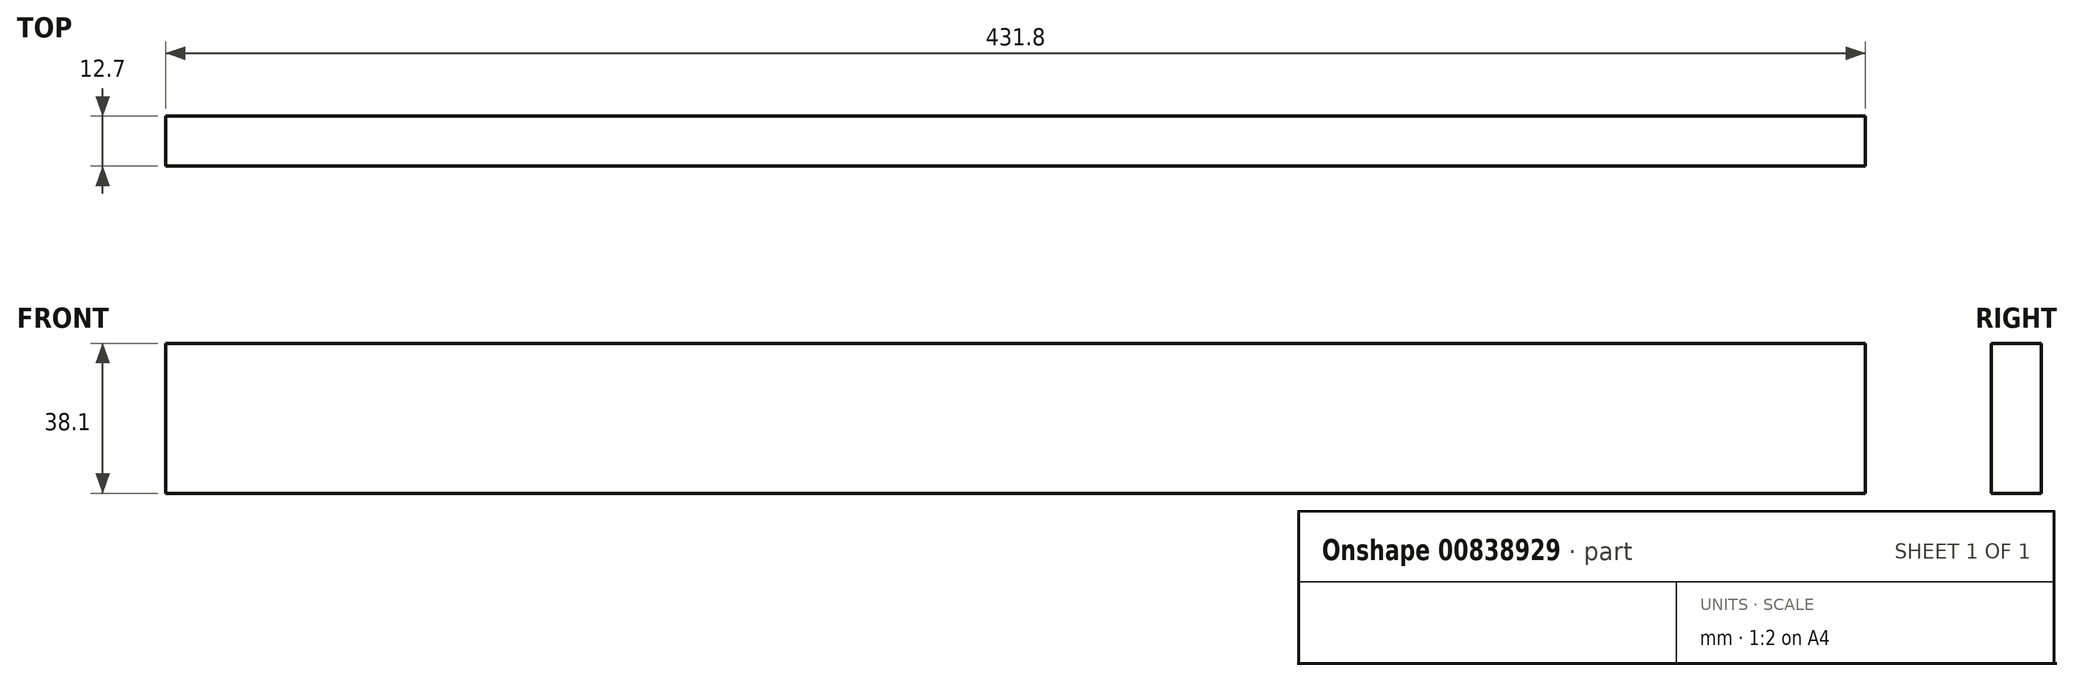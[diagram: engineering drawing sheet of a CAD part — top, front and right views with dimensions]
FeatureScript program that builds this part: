
annotation { "Feature Type Name" : "Feature", "Feature Type Description" : "" }
export const myFeature = defineFeature(function(context is Context, id is Id, definition is map)
    precondition{}
    {
        {
            var Q0;
            Q0=qCreatedBy(makeId("Front.planeOp"),FACE);
            var sketch = newSketch(context, id + "F0", { "sketchPlane" : qUnion([Q0])});
            skLineSegment(sketch, "E0", {"start": v(0, 0) * mm, "end": v(0, 38.1) * mm});
            skLineSegment(sketch, "E1", {"start": v(0, 38.1) * mm, "end": v(431.8, 38.1) * mm});
            skLineSegment(sketch, "E2", {"start": v(431.8, 38.1) * mm, "end": v(431.8, 0) * mm});
            skLineSegment(sketch, "E3", {"start": v(431.8, 0) * mm, "end": v(0, 0) * mm});
            skSolve(sketch);
        }
        {
            var Q0;
            Q0 = qSketchRegion(id + "F0", true);
            extrude(context, id + "F1", {"entities" : qUnion([Q0]), "depth" : 12.7 * mm, "offsetDistance" : 25.4 * mm});
        }
    });
